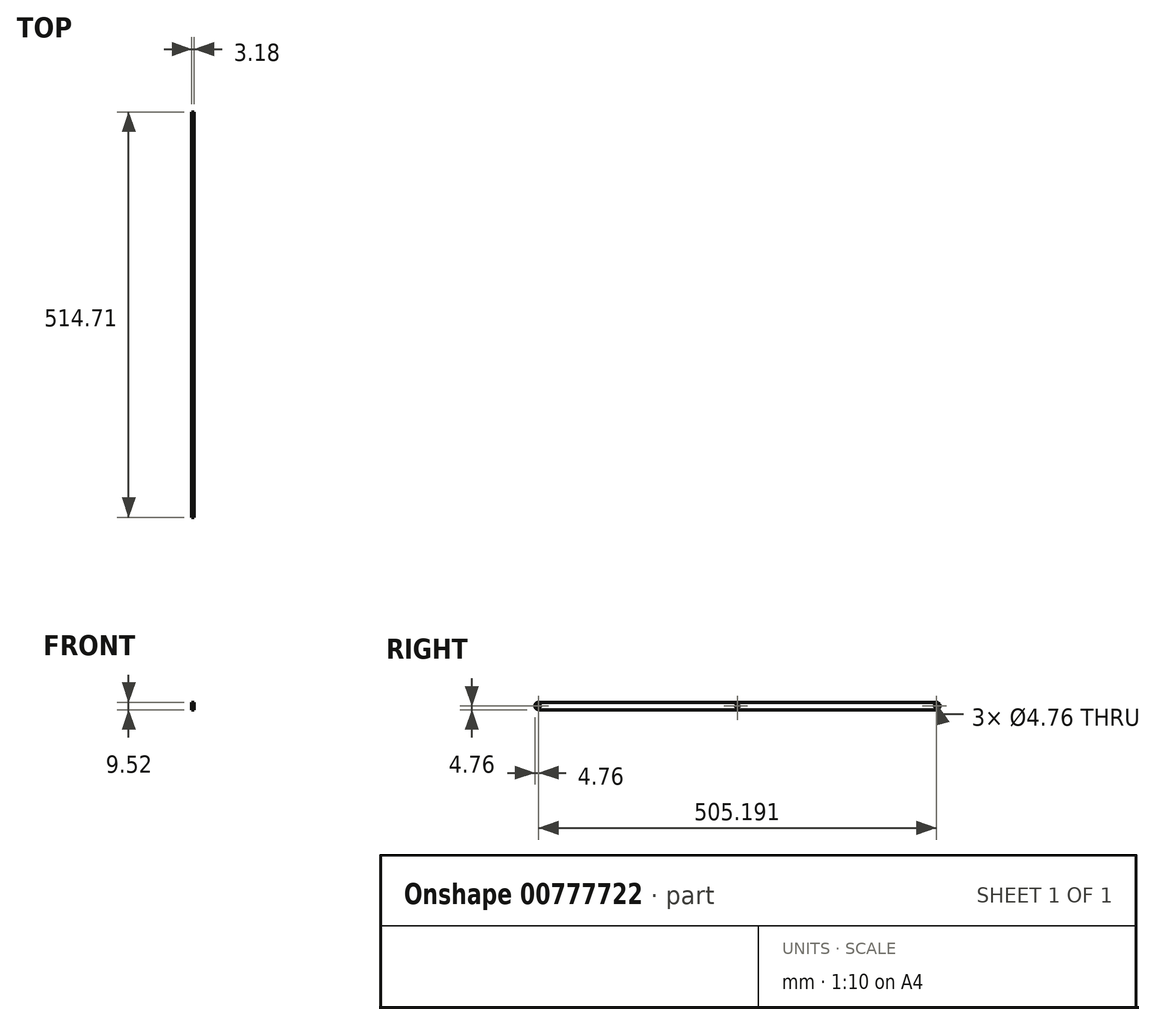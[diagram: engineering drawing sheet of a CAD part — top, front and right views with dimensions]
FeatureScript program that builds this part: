
annotation { "Feature Type Name" : "Feature", "Feature Type Description" : "" }
export const myFeature = defineFeature(function(context is Context, id is Id, definition is map)
    precondition{}
    {
        {
            var Q0;
            Q0=qCreatedBy(makeId("Right.planeOp"),FACE);
            var sketch = newSketch(context, id + "F0", { "sketchPlane" : qUnion([Q0])});
            skLineSegment(sketch, "E0.bottom", {"start": v(0, 4.76) * mm, "end": v(505.2, 4.76) * mm});
            skLineSegment(sketch, "E0.top", {"start": v(0, -4.76) * mm, "end": v(505.2, -4.76) * mm});
            skArc(sketch, "E1.filletArc", {"start": v(0, 4.76) * mm, "mid": v(-4.76, 0) * mm, "end": v(0, -4.76) * mm});
            skArc(sketch, "E2.filletArc", {"start": v(505.2, -4.76) * mm, "mid": v(509.95, 0) * mm, "end": v(505.2, 4.76) * mm});
            skCircle(sketch, "E3", {"center": v(0, 0) * mm, "radius": 2.38 * mm});
            skCircle(sketch, "E4", {"center": v(505.2, 0) * mm, "radius": 2.38 * mm});
            skCircle(sketch, "E5", {"center": v(252.6, 0) * mm, "radius": 2.38 * mm});
            skSolve(sketch);
        }
        {
            var Q0;
            Q0=qSketchRegion(id+"F0",true);
            extrude(context, id + "F1", {"entities" : qUnion([Q0]), "depth" : 3.17 * mm, "offsetDistance" : 25.4 * mm});
        }
    });
